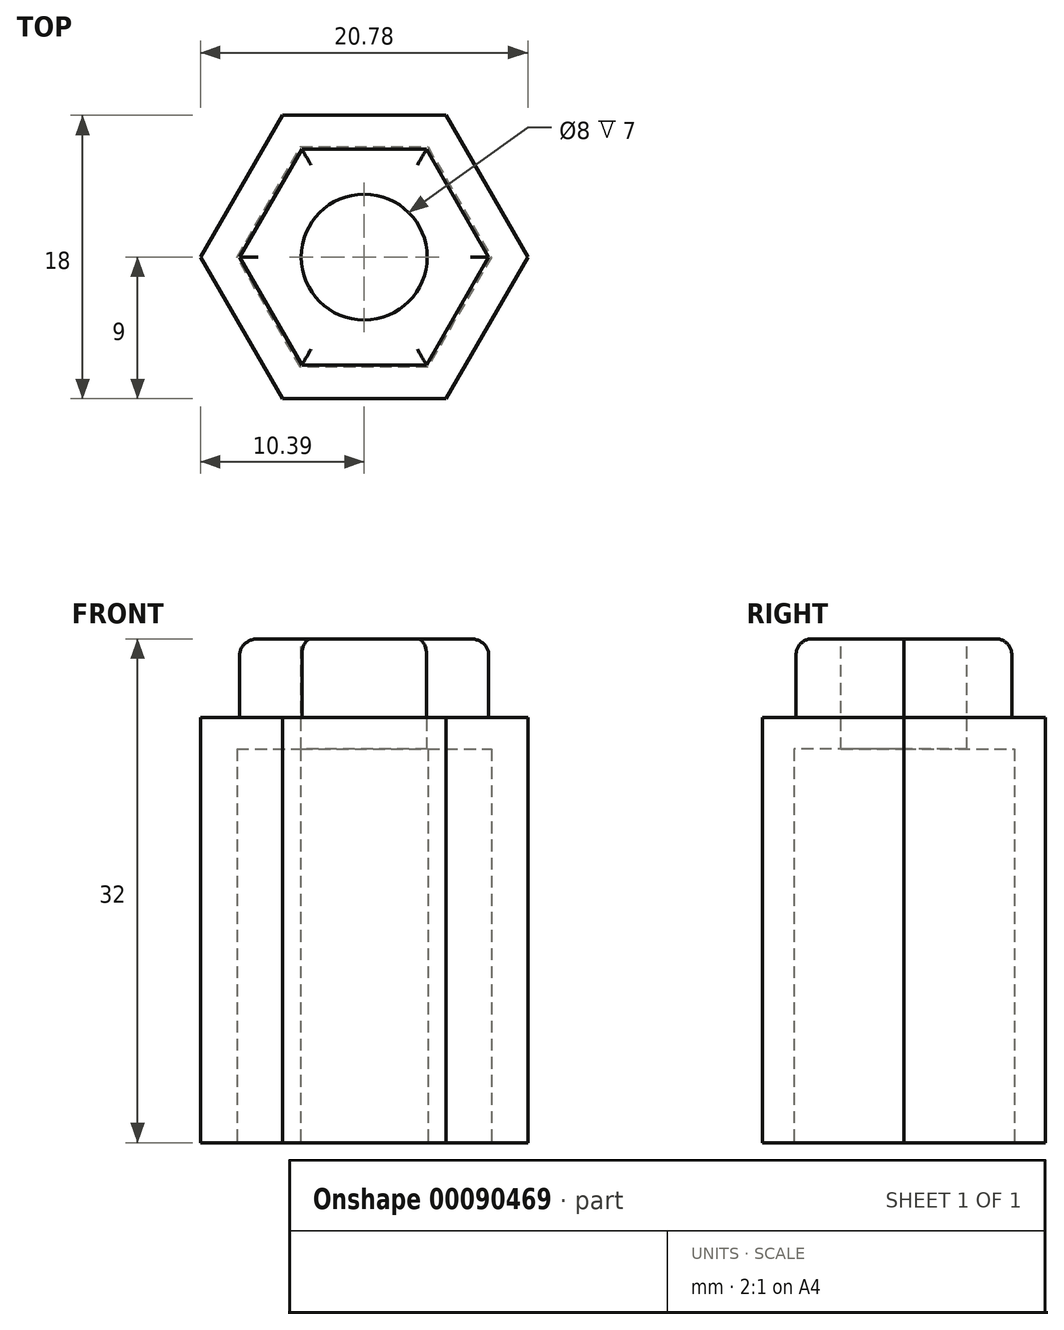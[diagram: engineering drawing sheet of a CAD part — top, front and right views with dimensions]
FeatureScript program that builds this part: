
annotation { "Feature Type Name" : "Feature", "Feature Type Description" : "" }
export const myFeature = defineFeature(function(context is Context, id is Id, definition is map)
    precondition{}
    {
        {
            var Q0;
            Q0=qCreatedBy(makeId("Top.planeOp"),FACE);
            var sketch = newSketch(context, id + "F0", { "sketchPlane" : qUnion([Q0])});
            skCircle(sketch, "E0.cCircle", {"center": v(0, 0) * mm, "radius": 7 * mm, "construction": true});
            skLineSegment(sketch, "E0.0", {"start": v(-4.04, 7) * mm, "end": v(4.04, 7) * mm});
            skLineSegment(sketch, "E0.1", {"start": v(4.04, 7) * mm, "end": v(8.08, 0) * mm});
            skLineSegment(sketch, "E0.2", {"start": v(8.08, 0) * mm, "end": v(4.04, -7) * mm});
            skLineSegment(sketch, "E0.3", {"start": v(4.04, -7) * mm, "end": v(-4.04, -7) * mm});
            skLineSegment(sketch, "E0.4", {"start": v(-4.04, -7) * mm, "end": v(-8.08, 0) * mm});
            skLineSegment(sketch, "E0.5", {"start": v(-8.08, 0) * mm, "end": v(-4.04, 7) * mm});
            skPoint(sketch, "E0.0.midPoint", {"position": v(0, 7) * mm});
            skCircle(sketch, "E1.cCircle", {"center": v(0, 0) * mm, "radius": 9 * mm, "construction": true});
            skLineSegment(sketch, "E1.0", {"start": v(-5.2, 9) * mm, "end": v(5.2, 9) * mm});
            skLineSegment(sketch, "E1.1", {"start": v(5.2, 9) * mm, "end": v(10.4, 0) * mm});
            skLineSegment(sketch, "E1.2", {"start": v(10.4, 0) * mm, "end": v(5.2, -9) * mm});
            skLineSegment(sketch, "E1.3", {"start": v(5.2, -9) * mm, "end": v(-5.2, -9) * mm});
            skLineSegment(sketch, "E1.4", {"start": v(-5.2, -9) * mm, "end": v(-10.4, 0) * mm});
            skLineSegment(sketch, "E1.5", {"start": v(-10.4, 0) * mm, "end": v(-5.2, 9) * mm});
            skPoint(sketch, "E1.0.midPoint", {"position": v(0, 9) * mm});
            skSolve(sketch);
        }
        {
            var Q0;
            Q0 = qSketchRegion(id + "F0", true);
            extrude(context, id + "F1", {"entities" : qUnion([Q0]), "depth" : 27 * mm});
        }
        {
            var Q0;
            Q0=makeQuery(id+"F1.opExtrude","CAP_FACE",FACE,{"disambiguationData":[OSD([sQuery(id+"F0.wireOp",EDGE,"E0.0"),sQuery(id+"F0.wireOp",EDGE,"E0.1"),sQuery(id+"F0.wireOp",EDGE,"E0.2"),sQuery(id+"F0.wireOp",EDGE,"E0.3"),sQuery(id+"F0.wireOp",EDGE,"E0.4"),sQuery(id+"F0.wireOp",EDGE,"E0.5"),sQuery(id+"F0.wireOp",EDGE,"E1.0"),sQuery(id+"F0.wireOp",EDGE,"E1.1"),sQuery(id+"F0.wireOp",EDGE,"E1.2"),sQuery(id+"F0.wireOp",EDGE,"E1.3"),sQuery(id+"F0.wireOp",EDGE,"E1.4"),sQuery(id+"F0.wireOp",EDGE,"E1.5")])],"isStart":false});
            var sketch = newSketch(context, id + "F2", { "sketchPlane" : qUnion([Q0])});
            skCircle(sketch, "E2.cCircle", {"center": v(0, 0) * mm, "radius": 9 * mm, "construction": true});
            skLineSegment(sketch, "E2.0", {"start": v(-5.2, 9) * mm, "end": v(5.2, 9) * mm});
            skLineSegment(sketch, "E2.1", {"start": v(5.2, 9) * mm, "end": v(10.4, 0) * mm});
            skLineSegment(sketch, "E2.2", {"start": v(10.4, 0) * mm, "end": v(5.2, -9) * mm});
            skLineSegment(sketch, "E2.3", {"start": v(5.2, -9) * mm, "end": v(-5.2, -9) * mm});
            skLineSegment(sketch, "E2.4", {"start": v(-5.2, -9) * mm, "end": v(-10.4, 0) * mm});
            skLineSegment(sketch, "E2.5", {"start": v(-10.4, 0) * mm, "end": v(-5.2, 9) * mm});
            skPoint(sketch, "E2.0.midPoint", {"position": v(0, 9) * mm});
            skCircle(sketch, "E3", {"center": v(0, 0) * mm, "radius": 4 * mm});
            skSolve(sketch);
        }
        {
            var Q0;
            Q0 = qSketchRegion(id + "F2", true);
            extrude(context, id + "F3", {"entities" : qUnion([Q0]), "operationType" : NewBodyOperationType.ADD, "oppositeDirection" : true, "depth" : 2 * mm});
        }
        {
            var Q0;
            Q0=makeQuery(id+"F3.boolean.opBoolean","MERGE",FACE,{"derivedFrom":[makeQuery(id+"F1.opExtrude","CAP_FACE",FACE,{"disambiguationData":[OSD([sQuery(id+"F0.wireOp",EDGE,"E0.0"),sQuery(id+"F0.wireOp",EDGE,"E0.1"),sQuery(id+"F0.wireOp",EDGE,"E0.2"),sQuery(id+"F0.wireOp",EDGE,"E0.3"),sQuery(id+"F0.wireOp",EDGE,"E0.4"),sQuery(id+"F0.wireOp",EDGE,"E0.5"),sQuery(id+"F0.wireOp",EDGE,"E1.0"),sQuery(id+"F0.wireOp",EDGE,"E1.1"),sQuery(id+"F0.wireOp",EDGE,"E1.2"),sQuery(id+"F0.wireOp",EDGE,"E1.3"),sQuery(id+"F0.wireOp",EDGE,"E1.4"),sQuery(id+"F0.wireOp",EDGE,"E1.5")])],"isStart":false}),makeQuery(id+"F3.opExtrude","CAP_FACE",FACE,{"disambiguationData":[OSD([sQuery(id+"F2.wireOp",EDGE,"E2.0"),sQuery(id+"F2.wireOp",EDGE,"E2.1"),sQuery(id+"F2.wireOp",EDGE,"E2.2"),sQuery(id+"F2.wireOp",EDGE,"E2.3"),sQuery(id+"F2.wireOp",EDGE,"E2.4"),sQuery(id+"F2.wireOp",EDGE,"E2.5"),sQuery(id+"F2.wireOp",EDGE,"E3")])],"isStart":true})]});
            var sketch = newSketch(context, id + "F4", { "sketchPlane" : qUnion([Q0])});
            skCircle(sketch, "E4.cCircle", {"center": v(0, 0) * mm, "radius": 6.85 * mm, "construction": true});
            skLineSegment(sketch, "E4.0", {"start": v(-3.95, 6.85) * mm, "end": v(3.95, 6.85) * mm});
            skLineSegment(sketch, "E4.1", {"start": v(3.95, 6.85) * mm, "end": v(7.9, 0) * mm});
            skLineSegment(sketch, "E4.2", {"start": v(7.9, 0) * mm, "end": v(3.95, -6.85) * mm});
            skLineSegment(sketch, "E4.3", {"start": v(3.95, -6.85) * mm, "end": v(-3.95, -6.85) * mm});
            skLineSegment(sketch, "E4.4", {"start": v(-3.95, -6.85) * mm, "end": v(-7.9, 0) * mm});
            skLineSegment(sketch, "E4.5", {"start": v(-7.9, 0) * mm, "end": v(-3.95, 6.85) * mm});
            skPoint(sketch, "E4.0.midPoint", {"position": v(0, 6.85) * mm});
            skCircle(sketch, "E5", {"center": v(0, 0) * mm, "radius": 4 * mm});
            skSolve(sketch);
        }
        {
            var Q0;
            Q0=makeQuery(id+"F4.imprint","IMPRINT",FACE,{"disambiguationData":[TD([[makeQuery(id+"F4.imprint","IMPRINT",EDGE,{"derivedFrom":sQuery(id+"F4.wireOp",EDGE,"E4.0")}),-1.0]])]});
            extrude(context, id + "F5", {"entities" : qUnion([Q0]), "operationType" : NewBodyOperationType.ADD, "depth" : 5 * mm});
        }
        {
            var Q0;
            Q0=makeQuery(id+"F5.opExtrude","CAP_EDGE",EDGE,{"disambiguationData":[OSD([sQuery(id+"F4.wireOp",EDGE,"E4.0")])],"isStart":false});
            var Q1;
            Q1=makeQuery(id+"F5.opExtrude","CAP_EDGE",EDGE,{"disambiguationData":[OSD([sQuery(id+"F4.wireOp",EDGE,"E4.5")])],"isStart":false});
            var Q2;
            Q2=makeQuery(id+"F5.opExtrude","CAP_EDGE",EDGE,{"disambiguationData":[OSD([sQuery(id+"F4.wireOp",EDGE,"E4.4")])],"isStart":false});
            var Q3;
            Q3=makeQuery(id+"F5.opExtrude","CAP_EDGE",EDGE,{"disambiguationData":[OSD([sQuery(id+"F4.wireOp",EDGE,"E4.3")])],"isStart":false});
            var Q4;
            Q4=makeQuery(id+"F5.opExtrude","CAP_EDGE",EDGE,{"disambiguationData":[OSD([sQuery(id+"F4.wireOp",EDGE,"E4.2")])],"isStart":false});
            var Q5;
            Q5=makeQuery(id+"F5.opExtrude","CAP_EDGE",EDGE,{"disambiguationData":[OSD([sQuery(id+"F4.wireOp",EDGE,"E4.1")])],"isStart":false});
            fillet(context, id + "F6", {"entities" : qUnion([Q0, Q1, Q2, Q3, Q4, Q5]), "radius" : 1 * mm, "tangentPropagation" : true, "allowEdgeOverflow" : false});
        }
    });
